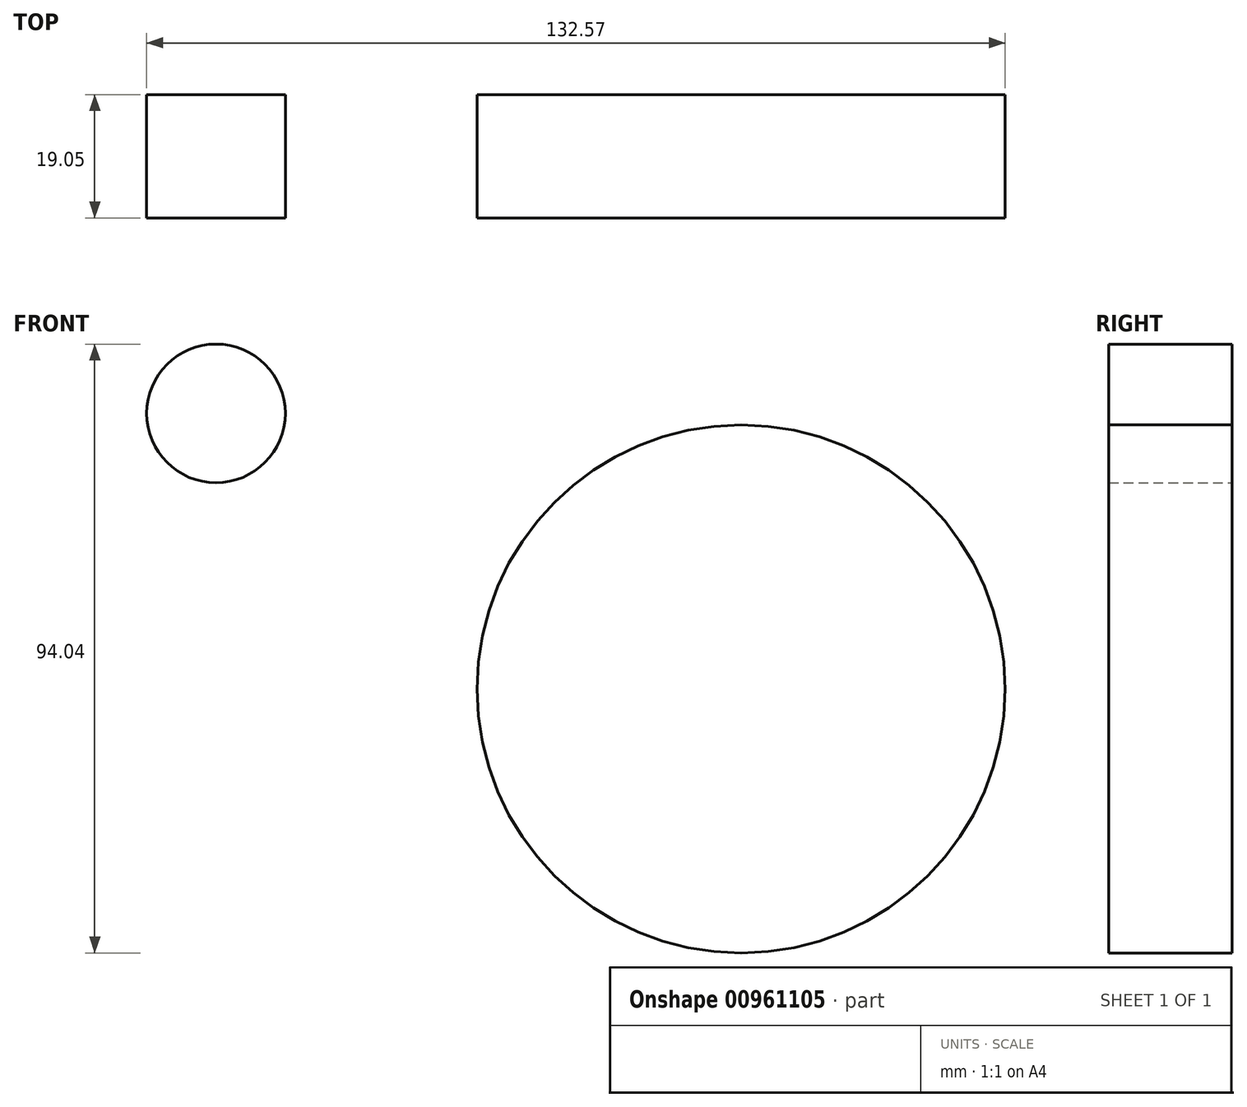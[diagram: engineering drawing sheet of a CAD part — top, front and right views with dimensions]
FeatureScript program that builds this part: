
annotation { "Feature Type Name" : "Feature", "Feature Type Description" : "" }
export const myFeature = defineFeature(function(context is Context, id is Id, definition is map)
    precondition{}
    {
        {
            var Q0;
            Q0=qCreatedBy(makeId("Front.planeOp"),FACE);
            var sketch = newSketch(context, id + "F0", { "sketchPlane" : qUnion([Q0])});
            skCircle(sketch, "E0", {"center": v(0, 0) * mm, "radius": 40.77 * mm});
            skSolve(sketch);
        }
        {
            var Q0;
            Q0=qCreatedBy(makeId("Front.planeOp"),FACE);
            var sketch = newSketch(context, id + "F1", { "sketchPlane" : qUnion([Q0])});
            skCircle(sketch, "E1", {"center": v(-81.1, 42.57) * mm, "radius": 10.7 * mm});
            skSolve(sketch);
        }
        {
            var Q0;
            Q0=makeQuery(id+"F1.imprint","IMPRINT",FACE,{"disambiguationData":[TD([[makeQuery(id+"F1.imprint","IMPRINT",EDGE,{"derivedFrom":sQuery(id+"F1.wireOp",EDGE,"E1")}),1.0]])]});
            extrude(context, id + "F2", {"entities" : qUnion([Q0]), "depth" : 19.05 * mm, "offsetDistance" : 25.4 * mm});
        }
        {
            var Q0;
            Q0=makeQuery(id+"F0.imprint","IMPRINT",FACE,{"disambiguationData":[TD([[makeQuery(id+"F0.imprint","IMPRINT",EDGE,{"derivedFrom":sQuery(id+"F0.wireOp",EDGE,"E0")}),1.0]])]});
            extrude(context, id + "F3", {"entities" : qUnion([Q0]), "depth" : 19.05 * mm, "offsetDistance" : 25.4 * mm});
        }
    });
